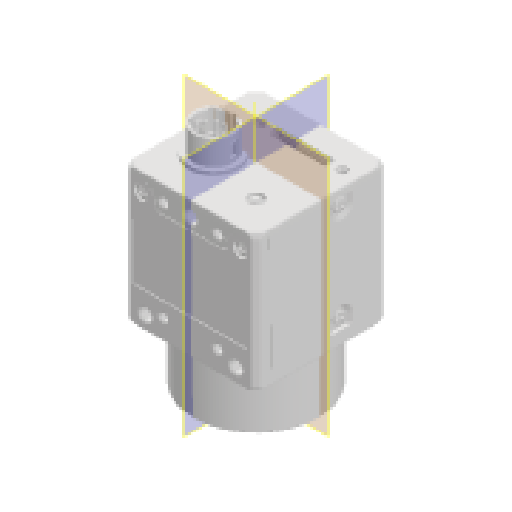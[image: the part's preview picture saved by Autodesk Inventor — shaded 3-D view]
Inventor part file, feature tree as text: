
AUTODESK INVENTOR PART (.ipt)
format: ipt  version: 2024.1 (Build 281209000, 209)  size: 2,924,544 bytes
history: native  units: mm
features: plane x2, other x1, imported_body x1
ambient origin geometry x8: Origin, YZ Plane, XZ Plane, XY Plane, X Axis, Y Axis, Z Axis, Center Point
bodies: Volumenkörper1 (feature_tree)
feature tree (4):
  plane  "Arbeitsebene1"
  plane  "Arbeitsebene2"
  other  "Arbeitsachse1"
  imported_body  "Basis1"
